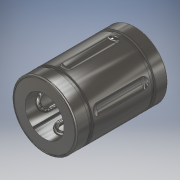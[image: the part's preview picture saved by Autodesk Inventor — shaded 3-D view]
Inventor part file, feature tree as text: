
AUTODESK INVENTOR PART (.ipt)
format: ipt  version: 2019 (Build 230136000, 136)  size: 1,567,744 bytes
history: native  units: in
note: dims shown in document units (in); Inventor stores cm internally (conversion verified against a paired STEP export)
features: extrude x2, fillet x1
ambient origin geometry x8: Origin, YZ Plane, XZ Plane, XY Plane, X Axis, Y Axis, Z Axis, Center Point
bodies: Solid1 (feature_tree), Solid2 (feature_tree), Solid3 (feature_tree)
feature tree (3):
  fillet  "Fillet5"  [1 undecoded]
  extrude  "Extrude5"  [1 undecoded]
  extrude  "Extrude6"  [1 undecoded]
note: 3 required parameter values undecoded (feature->parameter linkage not recoverable at this tier; creation-order binding heuristic only, values carry confidence <= 0.55)
